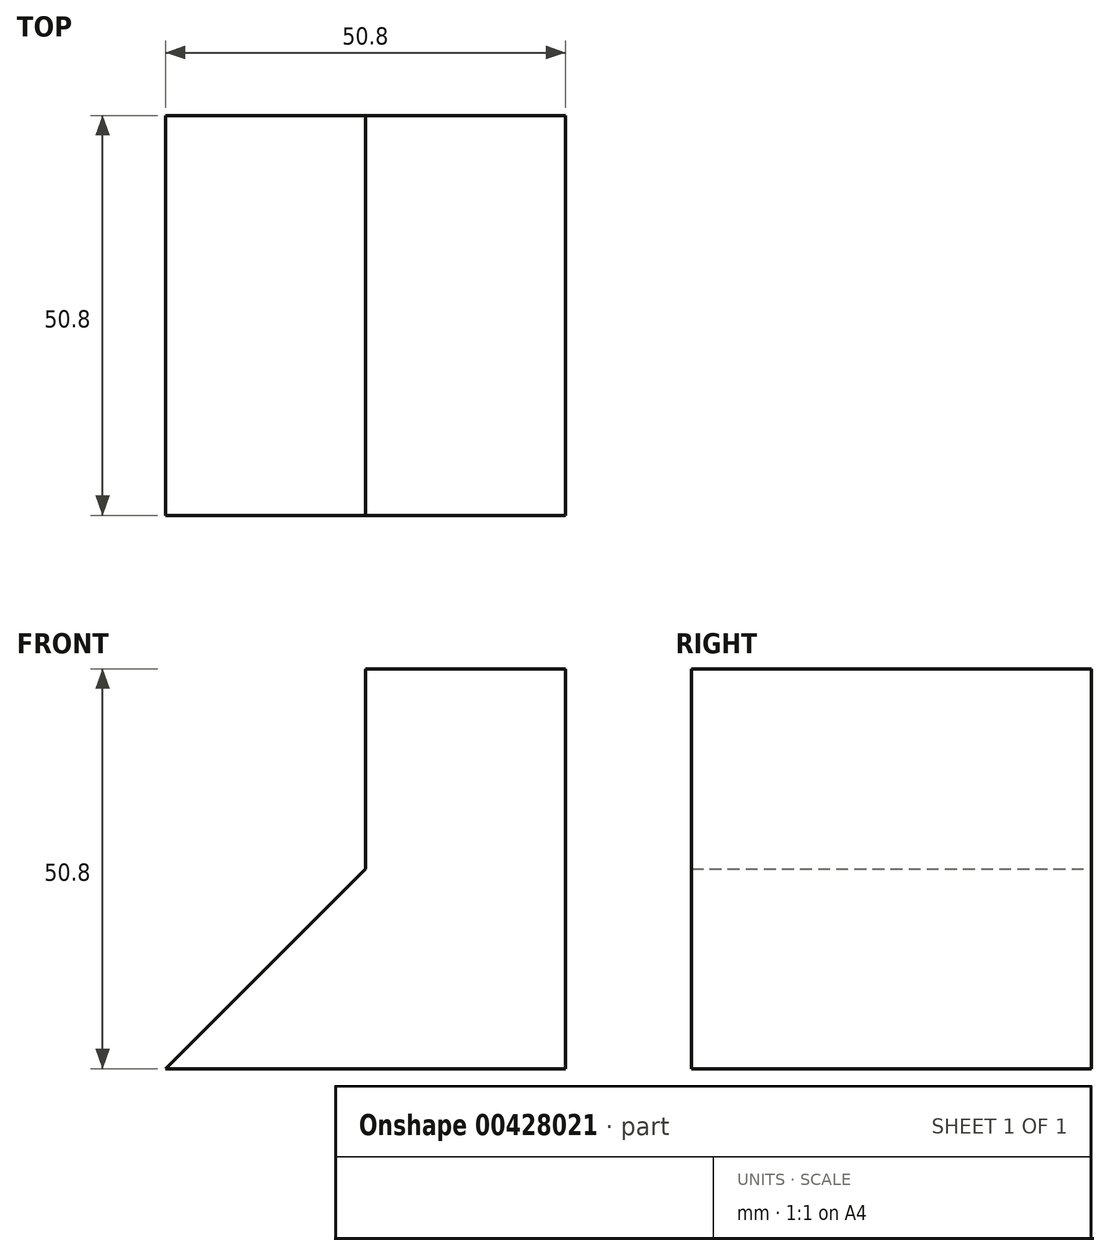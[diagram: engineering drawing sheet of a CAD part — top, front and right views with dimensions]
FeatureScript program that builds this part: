
annotation { "Feature Type Name" : "Feature", "Feature Type Description" : "" }
export const myFeature = defineFeature(function(context is Context, id is Id, definition is map)
    precondition{}
    {
        {
            var Q0;
            Q0=qCreatedBy(makeId("Front.planeOp"),FACE);
            var sketch = newSketch(context, id + "F0", { "sketchPlane" : qUnion([Q0])});
            skLineSegment(sketch, "E0", {"start": v(0, 0) * mm, "end": v(0, 50.8) * mm});
            skLineSegment(sketch, "E1", {"start": v(0, 50.8) * mm, "end": v(-25.4, 50.8) * mm});
            skLineSegment(sketch, "E2", {"start": v(0, 0) * mm, "end": v(-50.8, 0) * mm});
            skLineSegment(sketch, "E3", {"start": v(-25.4, 50.8) * mm, "end": v(-25.4, 25.4) * mm});
            skLineSegment(sketch, "E4", {"start": v(-25.4, 25.4) * mm, "end": v(-50.8, 0) * mm});
            skSolve(sketch);
        }
        {
            var Q0;
            Q0 = qSketchRegion(id + "F0", true);
            extrude(context, id + "F1", {"entities" : qUnion([Q0]), "depth" : 50.8 * mm});
        }
    });
